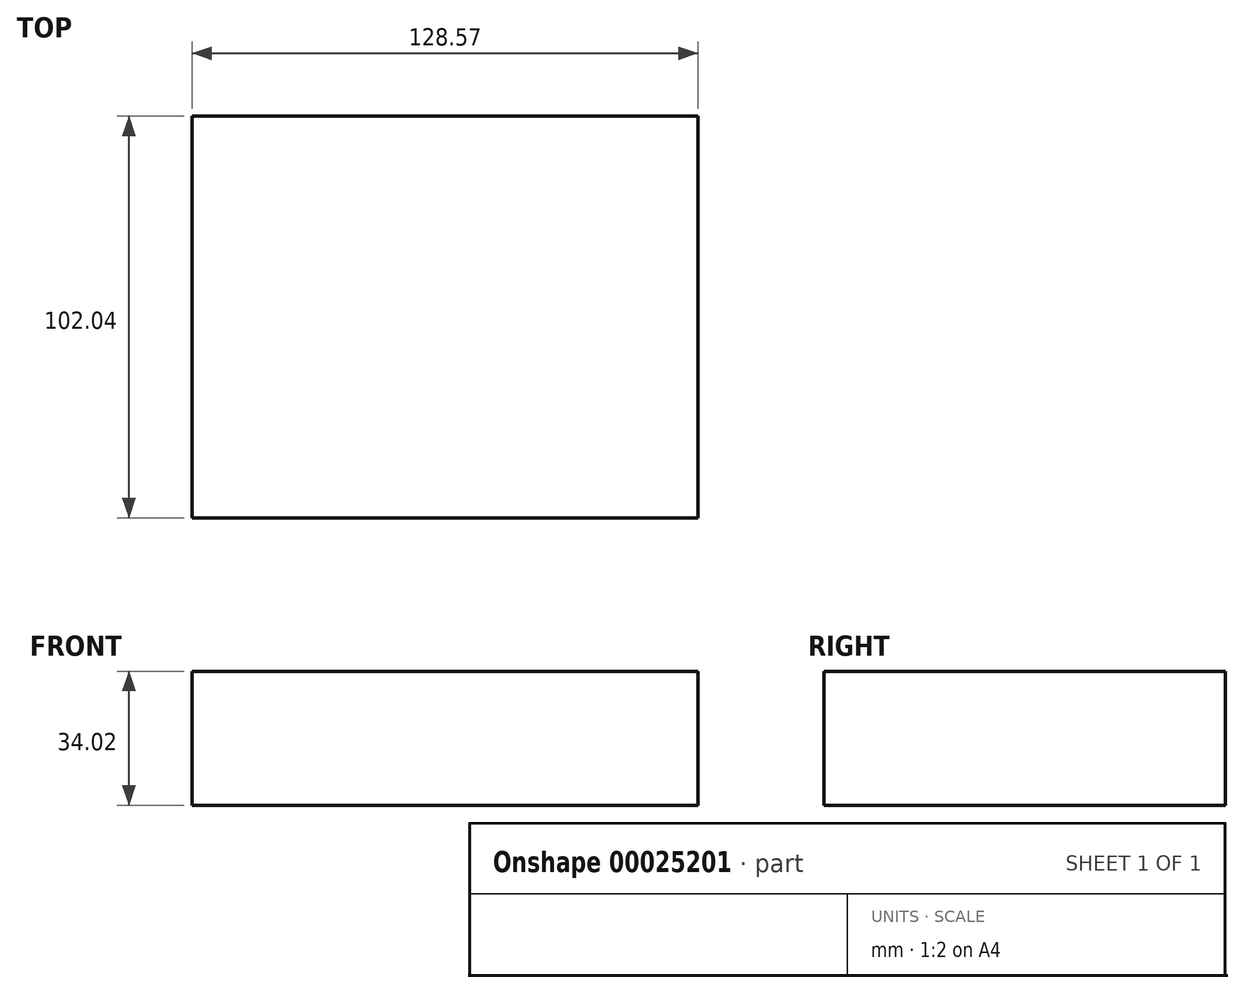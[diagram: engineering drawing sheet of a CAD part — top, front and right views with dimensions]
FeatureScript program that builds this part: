
annotation { "Feature Type Name" : "Feature", "Feature Type Description" : "" }
export const myFeature = defineFeature(function(context is Context, id is Id, definition is map)
    precondition{}
    {
        {
            var Q0;
            Q0=qCreatedBy(makeId("Top.planeOp"),FACE);
            var sketch = newSketch(context, id + "F0", { "sketchPlane" : qUnion([Q0])});
            skLineSegment(sketch, "E0.bottom", {"start": v(-68.74, 44.65) * mm, "end": v(59.83, 44.65) * mm});
            skLineSegment(sketch, "E0.top", {"start": v(-68.74, -57.39) * mm, "end": v(59.83, -57.39) * mm});
            skLineSegment(sketch, "E0.left", {"start": v(-68.74, 44.65) * mm, "end": v(-68.74, -57.39) * mm});
            skLineSegment(sketch, "E0.right", {"start": v(59.83, 44.65) * mm, "end": v(59.83, -57.39) * mm});
            skSolve(sketch);
        }
        {
            var Q0;
            Q0=makeQuery(id+"F0.imprint","IMPRINT",FACE,{"disambiguationData":[TD([[makeQuery(id+"F0.imprint","IMPRINT",EDGE,{"derivedFrom":sQuery(id+"F0.wireOp",EDGE,"E0.bottom")}),-1.0]])]});
            extrude(context, id + "F1", {"entities" : qUnion([Q0]), "depth" : 59.42 * mm});
        }
        {
            var Q0;
            Q0=makeQuery(id+"F1.opExtrude","CAP_FACE",FACE,{"disambiguationData":[OSD([sQuery(id+"F0.wireOp",EDGE,"E0.bottom"),sQuery(id+"F0.wireOp",EDGE,"E0.top"),sQuery(id+"F0.wireOp",EDGE,"E0.left"),sQuery(id+"F0.wireOp",EDGE,"E0.right")])],"isStart":false});
            var sketch = newSketch(context, id + "F2", { "sketchPlane" : qUnion([Q0])});
            skLineSegment(sketch, "E1.bottom", {"start": v(-39.06, -26.99) * mm, "end": v(21.8, -26.99) * mm});
            skLineSegment(sketch, "E1.top", {"start": v(-39.06, 13) * mm, "end": v(21.8, 13) * mm});
            skLineSegment(sketch, "E1.left", {"start": v(-39.06, -26.99) * mm, "end": v(-39.06, 13) * mm});
            skLineSegment(sketch, "E1.right", {"start": v(21.8, -26.99) * mm, "end": v(21.8, 13) * mm});
            skSolve(sketch);
        }
        {
            var Q0;
            Q0=makeQuery(id+"F2.imprint","IMPRINT",FACE,{"disambiguationData":[TD([[makeQuery(id+"F2.imprint","IMPRINT",EDGE,{"derivedFrom":sQuery(id+"F2.wireOp",EDGE,"E1.bottom")}),1.0]])]});
            extrude(context, id + "F3", {"entities" : qUnion([Q0]), "operationType" : NewBodyOperationType.REMOVE, "oppositeDirection" : true, "depth" : 25.4 * mm});
        }
        {
            var Q0;
            Q0=makeQuery(id+"F1.opExtrude","CAP_FACE",FACE,{"disambiguationData":[OSD([sQuery(id+"F0.wireOp",EDGE,"E0.bottom"),sQuery(id+"F0.wireOp",EDGE,"E0.top"),sQuery(id+"F0.wireOp",EDGE,"E0.left"),sQuery(id+"F0.wireOp",EDGE,"E0.right")])],"isStart":false});
            extrude(context, id + "F4", {"entities" : qUnion([Q0]), "operationType" : NewBodyOperationType.REMOVE, "oppositeDirection" : true, "depth" : 25.4 * mm});
        }
    });
